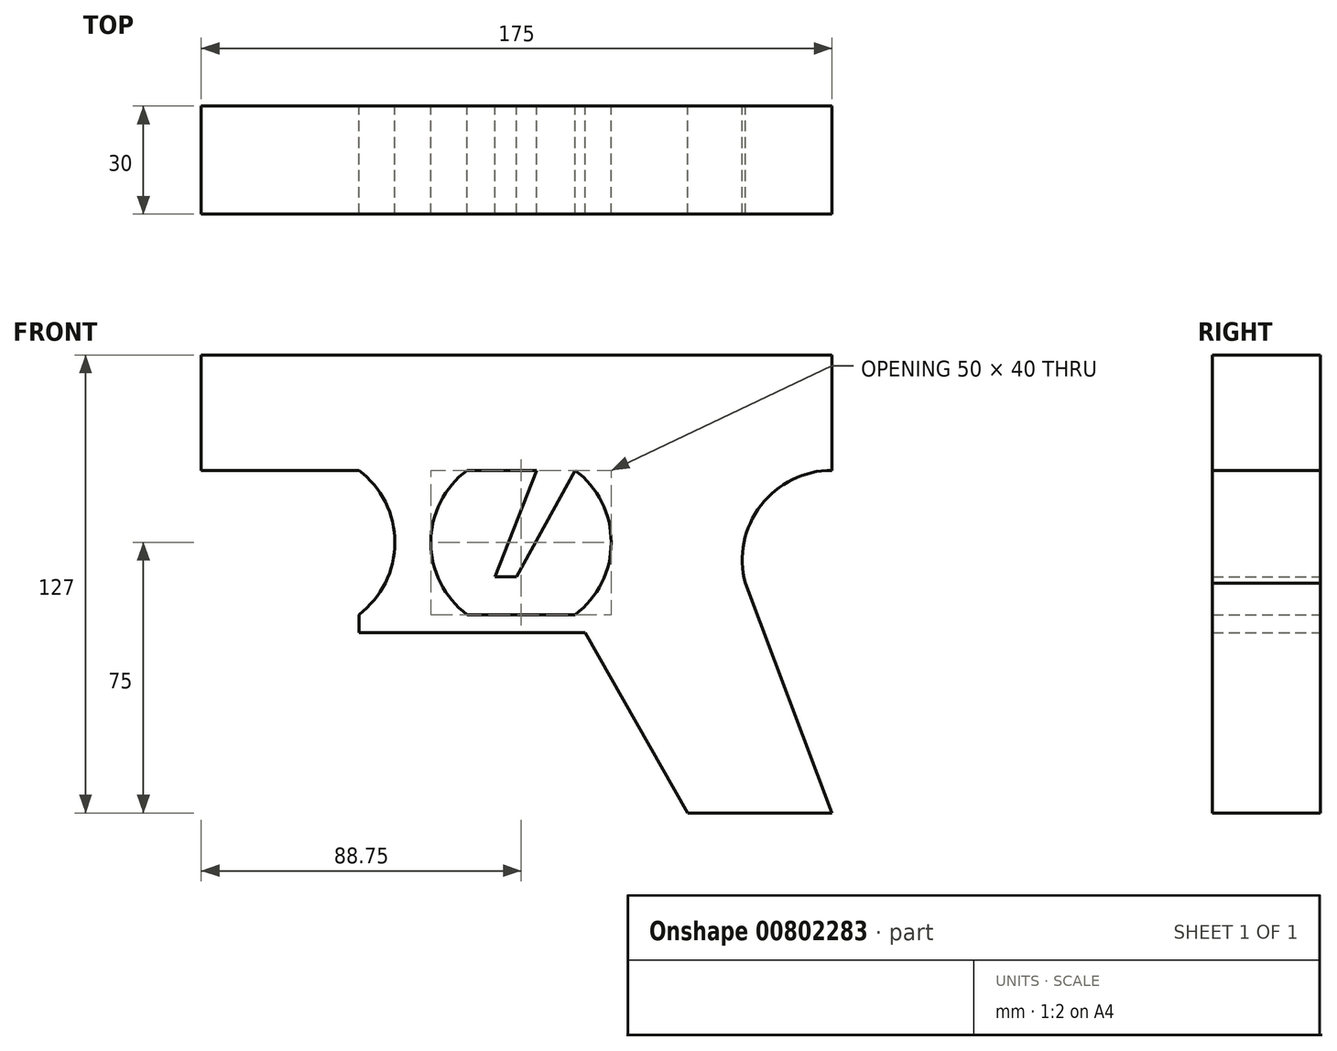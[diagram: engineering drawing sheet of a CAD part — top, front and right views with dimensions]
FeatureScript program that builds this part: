
annotation { "Feature Type Name" : "Feature", "Feature Type Description" : "" }
export const myFeature = defineFeature(function(context is Context, id is Id, definition is map)
    precondition{}
    {
        {
            var Q0;
            Q0=qCreatedBy(makeId("Front.planeOp"),FACE);
            var sketch = newSketch(context, id + "F0", { "sketchPlane" : qUnion([Q0])});
            skLineSegment(sketch, "E0.bottom", {"start": v(87.5, -16) * mm, "end": v(-87.5, -16) * mm});
            skLineSegment(sketch, "E0.top", {"start": v(87.5, 16) * mm, "end": v(-87.5, 16) * mm});
            skLineSegment(sketch, "E0.left", {"start": v(87.5, -16) * mm, "end": v(87.5, 16) * mm});
            skLineSegment(sketch, "E0.right", {"start": v(-87.5, -16) * mm, "end": v(-87.5, 16) * mm});
            skPoint(sketch, "E0.middle", {"position": v(0, 0) * mm});
            skLineSegment(sketch, "E1", {"start": v(87.5, 16) * mm, "end": v(87.5, -111) * mm});
            skLineSegment(sketch, "E2", {"start": v(87.5, -111) * mm, "end": v(47.5, -111) * mm});
            skLineSegment(sketch, "E3", {"start": v(47.5, -111) * mm, "end": v(16.25, -56) * mm});
            skLineSegment(sketch, "E4", {"start": v(16.25, -56) * mm, "end": v(-43.75, -56) * mm});
            skLineSegment(sketch, "E5", {"start": v(-87.5, -16) * mm, "end": v(0, -16) * mm});
            skLineSegment(sketch, "E6", {"start": v(-43.75, -16) * mm, "end": v(-43.75, -56) * mm});
            skLineSegment(sketch, "E7", {"start": v(87.5, -111) * mm, "end": v(63.45, -47.31) * mm});
            skArc(sketch, "E8", {"start": v(87.5, -16) * mm, "mid": v(67.76, -25.73) * mm, "end": v(63.45, -47.31) * mm});
            skArc(sketch, "E9", {"start": v(-43.75, -56) * mm, "mid": v(-33.75, -36) * mm, "end": v(-43.75, -16) * mm});
            skArc(sketch, "E10", {"start": v(-13.75, -16) * mm, "mid": v(-23.75, -36) * mm, "end": v(-13.75, -56) * mm});
            skArc(sketch, "E11", {"start": v(16.25, -56) * mm, "mid": v(26.25, -36) * mm, "end": v(16.25, -16) * mm});
            skLineSegment(sketch, "E12", {"start": v(16.25, -16) * mm, "end": v(0, -45.48) * mm});
            skPoint(sketch, "E12.endSnap0", {"position": v(0, 16) * mm});
            skLineSegment(sketch, "E13", {"start": v(0, -45.48) * mm, "end": v(-6.02, -45.48) * mm});
            skLineSegment(sketch, "E14", {"start": v(-6.02, -45.48) * mm, "end": v(5.63, -16) * mm});
            skLineSegment(sketch, "E15.bottom", {"start": v(-43.75, -56) * mm, "end": v(19.1, -56) * mm});
            skLineSegment(sketch, "E15.top", {"start": v(-43.75, -61) * mm, "end": v(19.1, -61) * mm});
            skLineSegment(sketch, "E15.left", {"start": v(-43.75, -56) * mm, "end": v(-43.75, -61) * mm});
            skLineSegment(sketch, "E15.right", {"start": v(19.1, -56) * mm, "end": v(19.1, -61) * mm});
            skSolve(sketch);
        }
        {
            var Q0;
            {var subQ0=sQuery(id+"F0.wireOp",EDGE,"E9");Q0=makeQuery(id+"F0.imprint","IMPRINT",FACE,{"disambiguationData":[TD([[makeQuery(id+"F0.imprint","IMPRINT",EDGE,{"derivedFrom":subQ0}),-1.0]])]});}
            var Q1;
            {var subQ2=sQuery(id+"F0.wireOp",EDGE,"E2");Q1=makeQuery(id+"F0.imprint","IMPRINT",FACE,{"disambiguationData":[TD([[makeQuery(id+"F0.imprint","IMPRINT",EDGE,{"derivedFrom":subQ2}),-1.0]])]});}
            var Q2;
            Q2=makeQuery(id+"F0.imprint","IMPRINT",FACE,{"disambiguationData":[TD([[makeQuery(id+"F0.imprint","IMPRINT",EDGE,{"derivedFrom":sQuery(id+"F0.wireOp",EDGE,"E0.top")}),1.0]])]});
            var Q3;
            {var subQ0=sQuery(id+"F0.wireOp",EDGE,"E12");Q3=makeQuery(id+"F0.imprint","IMPRINT",FACE,{"disambiguationData":[TD([[makeQuery(id+"F0.imprint","IMPRINT",EDGE,{"derivedFrom":subQ0}),-1.0]])]});}
            var Q4;
            {var subQ0=sQuery(id+"F0.wireOp",EDGE,"E15.top");Q4=makeQuery(id+"F0.imprint","IMPRINT",FACE,{"disambiguationData":[TD([[makeQuery(id+"F0.imprint","IMPRINT",EDGE,{"derivedFrom":subQ0}),1.0]])]});}
            var Q5;
            {var subQ0=sQuery(id+"F0.wireOp",EDGE,"E15.bottom");Q5=makeQuery(id+"F0.imprint","IMPRINT",FACE,{"disambiguationData":[TD([[makeQuery(id+"F0.imprint","IMPRINT",EDGE,{"derivedFrom":subQ0}),-1.0]])]});}
            extrude(context, id + "F1", {"entities" : qUnion([Q0, Q1, Q2, Q3, Q4, Q5]), "depth" : 30 * mm, "offsetDistance" : 25 * mm});
        }
    });
